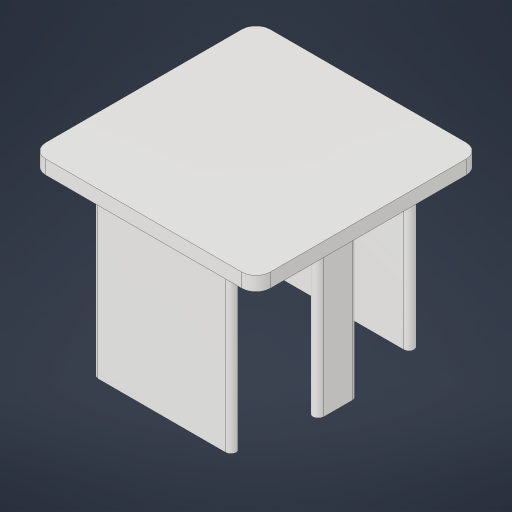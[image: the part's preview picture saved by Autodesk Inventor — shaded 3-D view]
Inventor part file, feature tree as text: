
AUTODESK INVENTOR PART (.ipt)
format: ipt  version: 2023.4 (Build 274418000, 418)  size: 224,768 bytes
history: native  units: in
note: dims shown in document units (in); Inventor stores cm internally (conversion verified against a paired STEP export)
features: extrude x2, fillet x2, sketch x1
ambient origin geometry x8: Origin, YZ Plane, XZ Plane, XY Plane, X Axis, Y Axis, Z Axis, Center Point
bodies: Solid1 (feature_tree)
feature tree (5):
  sketch  "Sketch1"  dims[d0=1.25in d1=2.0in d2=2.0in d3=1.477in d4=0.11in d5=1.25in d6=0.11in d7=0.37in d8=0.115in d10=0.01in d11=0.01in d12=0.125in d13=0.0in d14=1.5in d15=0.0in d16=0.125in d17=0.125in]
  extrude  "Extrusion1"  Depth=2.0in
  extrude  "Extrusion2"  Depth=2.0in
  fillet  "Fillet1"  Radius=1.477in
  fillet  "Fillet2"  Radius=0.11in
